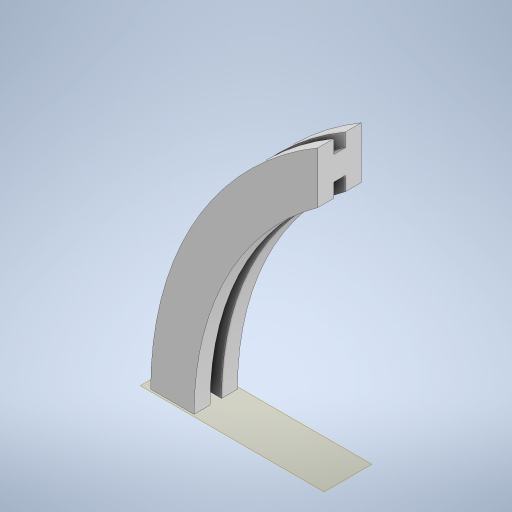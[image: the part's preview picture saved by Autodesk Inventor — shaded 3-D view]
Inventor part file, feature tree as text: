
AUTODESK INVENTOR PART (.ipt)
format: ipt  version: 2023 (Build 270158000, 158)  size: 278,528 bytes
history: native  units: mm
features: sketch x3, sweep x1, extrude x1
ambient origin geometry x8: Origin, YZ Plane, XZ Plane, XY Plane, X Axis, Y Axis, Z Axis, Center Point
bodies: Solid1 (feature_tree)
feature tree (5):
  sweep  "Sweep1"
  extrude  "Extrusion1"  Depth=8.0mm
  sketch  "Sketch1"  dims[d1=440.0mm d5=100.0mm]
  sketch  "Sketch2"  dims[d17=220.0mm d18=8.0mm]
  sketch  "Sketch3"  dims[d19=8.0mm d21=14.0mm d22=30.0mm d23=15.0mm d24=4.0mm d25=7.0mm d26=0.0mm d27=0.0mm d28=356.72745mm d29=304.295082mm d30=100.651459mm d31=0.0mm d32=0.0mm d33=0.0mm]
